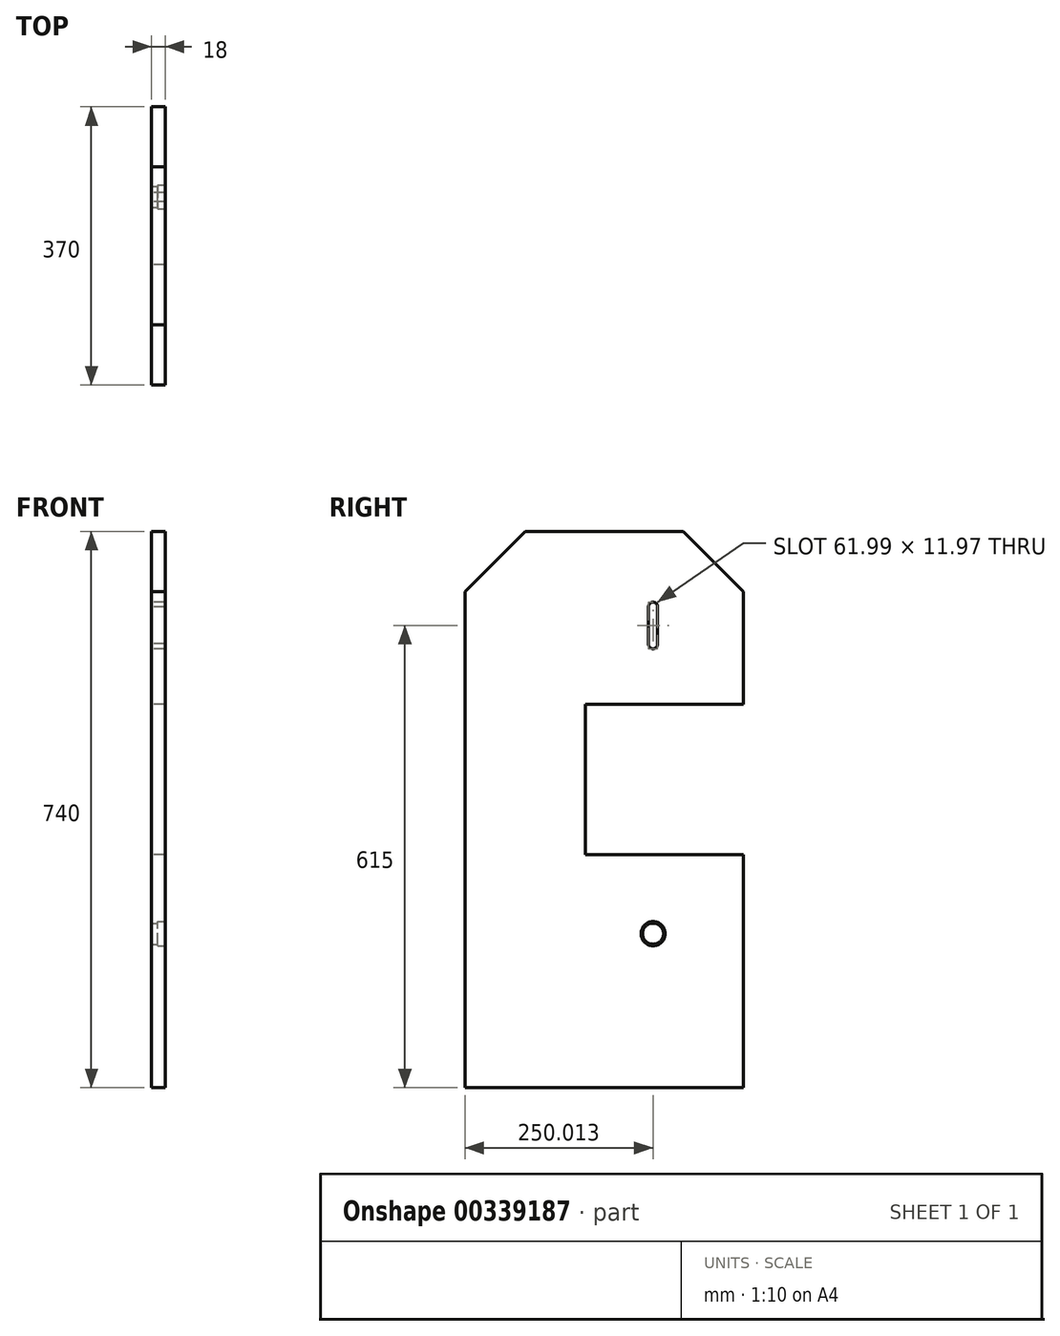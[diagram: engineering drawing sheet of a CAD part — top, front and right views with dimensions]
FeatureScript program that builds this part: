
annotation { "Feature Type Name" : "Feature", "Feature Type Description" : "" }
export const myFeature = defineFeature(function(context is Context, id is Id, definition is map)
    precondition{}
    {
        {
            var Q0;
            Q0=qCreatedBy(makeId("Right.planeOp"),FACE);
            var sketch = newSketch(context, id + "F0", { "sketchPlane" : qUnion([Q0])});
            skLineSegment(sketch, "E0", {"start": v(0, 0) * mm, "end": v(0, 740) * mm});
            skLineSegment(sketch, "E1", {"start": v(0, 740) * mm, "end": v(370, 740) * mm});
            skLineSegment(sketch, "E2", {"start": v(370, 740) * mm, "end": v(370, 510) * mm});
            skLineSegment(sketch, "E3", {"start": v(0, 0) * mm, "end": v(370, 0) * mm});
            skLineSegment(sketch, "E4", {"start": v(370, 0) * mm, "end": v(370, 310) * mm});
            skLineSegment(sketch, "E5", {"start": v(370, 310) * mm, "end": v(160, 310) * mm});
            skLineSegment(sketch, "E6", {"start": v(160, 310) * mm, "end": v(160, 510) * mm});
            skLineSegment(sketch, "E7", {"start": v(160, 510) * mm, "end": v(370, 510) * mm});
            skArc(sketch, "E8", {"start": v(256, 640) * mm, "mid": v(249.72, 646) * mm, "end": v(244.03, 639.44) * mm});
            skArc(sketch, "E9", {"start": v(244.03, 590.56) * mm, "mid": v(249.72, 584) * mm, "end": v(256, 590) * mm});
            skLineSegment(sketch, "E10", {"start": v(244.03, 640.56) * mm, "end": v(244.03, 589.44) * mm});
            skLineSegment(sketch, "E11", {"start": v(256, 640) * mm, "end": v(256, 590) * mm});
            skPoint(sketch, "E12", {"position": v(250, 205) * mm});
            skSolve(sketch);
        }
        {
            var Q0;
            Q0=makeQuery(id+"F0.imprint","IMPRINT",FACE,{"disambiguationData":[TD([[makeQuery(id+"F0.imprint","IMPRINT",EDGE,{"derivedFrom":sQuery(id+"F0.wireOp",EDGE,"E0")}),-1.0]])]});
            extrude(context, id + "F1", {"entities" : qUnion([Q0]), "depth" : 18 * mm});
        }
        {
            var Q0;
            Q0=makeQuery(id+"F1.opExtrude","SWEPT_EDGE",EDGE,{"disambiguationData":[OSD([sQuery(id+"F0.wireOp",EDGE,"E0"),sQuery(id+"F0.wireOp",EDGE,"E1")])]});
            var Q1;
            Q1=makeQuery(id+"F1.opExtrude","SWEPT_EDGE",EDGE,{"disambiguationData":[OSD([sQuery(id+"F0.wireOp",EDGE,"E1"),sQuery(id+"F0.wireOp",EDGE,"E2")])]});
            chamfer(context, id + "F2", {"entities" : qUnion([Q0, Q1]), "width" : 80 * mm, "tangentPropagation" : true});
        }
        {
            var Q0;
            Q0=makeQuery(id+"F1.opExtrude","CAP_FACE",FACE,{"disambiguationData":[OSD([sQuery(id+"F0.wireOp",EDGE,"E0"),sQuery(id+"F0.wireOp",EDGE,"E1"),sQuery(id+"F0.wireOp",EDGE,"E2"),sQuery(id+"F0.wireOp",EDGE,"E3"),sQuery(id+"F0.wireOp",EDGE,"E4"),sQuery(id+"F0.wireOp",EDGE,"E5"),sQuery(id+"F0.wireOp",EDGE,"E6"),sQuery(id+"F0.wireOp",EDGE,"E7"),sQuery(id+"F0.wireOp",EDGE,"E8"),sQuery(id+"F0.wireOp",EDGE,"E9"),sQuery(id+"F0.wireOp",EDGE,"E10"),sQuery(id+"F0.wireOp",EDGE,"E11")])],"isStart":false});
            var sketch = newSketch(context, id + "F3", { "sketchPlane" : qUnion([Q0])});
            skCircle(sketch, "E13", {"center": v(250, 205) * mm, "radius": 16 * mm});
            skSolve(sketch);
        }
        {
            var Q0;
            Q0=makeQuery(id+"F3.imprint","IMPRINT",FACE,{"disambiguationData":[TD([[makeQuery(id+"F3.imprint","IMPRINT",EDGE,{"derivedFrom":sQuery(id+"F3.wireOp",EDGE,"E13")}),1.0]])]});
            extrude(context, id + "F4", {"entities" : qUnion([Q0]), "operationType" : NewBodyOperationType.REMOVE, "oppositeDirection" : true, "depth" : 10 * mm});
        }
        {
            var Q0;
            Q0=makeQuery(id+"F1.opExtrude","CAP_FACE",FACE,{"disambiguationData":[OSD([sQuery(id+"F0.wireOp",EDGE,"E0"),sQuery(id+"F0.wireOp",EDGE,"E1"),sQuery(id+"F0.wireOp",EDGE,"E2"),sQuery(id+"F0.wireOp",EDGE,"E3"),sQuery(id+"F0.wireOp",EDGE,"E4"),sQuery(id+"F0.wireOp",EDGE,"E5"),sQuery(id+"F0.wireOp",EDGE,"E6"),sQuery(id+"F0.wireOp",EDGE,"E7"),sQuery(id+"F0.wireOp",EDGE,"E8"),sQuery(id+"F0.wireOp",EDGE,"E9"),sQuery(id+"F0.wireOp",EDGE,"E10"),sQuery(id+"F0.wireOp",EDGE,"E11")])],"isStart":false});
            var sketch = newSketch(context, id + "F5", { "sketchPlane" : qUnion([Q0])});
            skCircle(sketch, "E14", {"center": v(250, 205) * mm, "radius": 14 * mm});
            skSolve(sketch);
        }
        {
            var Q0;
            Q0=makeQuery(id+"F5.imprint","IMPRINT",FACE,{"disambiguationData":[TD([[makeQuery(id+"F5.imprint","IMPRINT",EDGE,{"derivedFrom":sQuery(id+"F5.wireOp",EDGE,"E14")}),1.0]])]});
            extrude(context, id + "F6", {"entities" : qUnion([Q0]), "operationType" : NewBodyOperationType.REMOVE, "oppositeDirection" : true, "depth" : 18 * mm});
        }
    });
